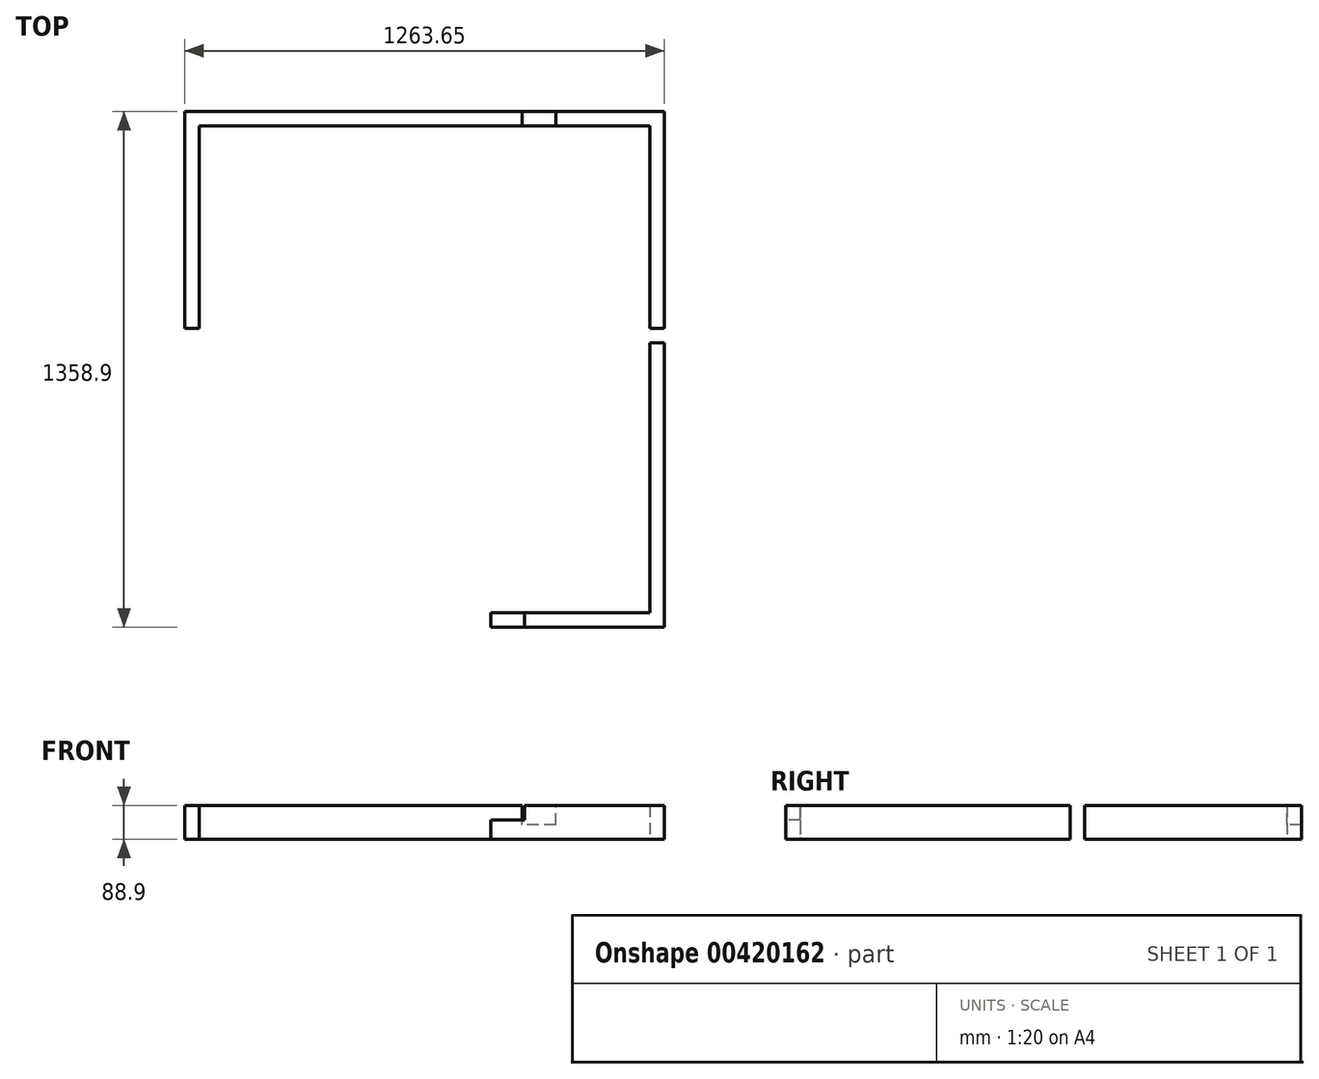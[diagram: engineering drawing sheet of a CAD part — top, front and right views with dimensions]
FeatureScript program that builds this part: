
annotation { "Feature Type Name" : "Feature", "Feature Type Description" : "" }
export const myFeature = defineFeature(function(context is Context, id is Id, definition is map)
    precondition{}
    {
        {
            var Q0;
            Q0=qCreatedBy(makeId("Top.planeOp"),FACE);
            var sketch = newSketch(context, id + "F0", { "sketchPlane" : qUnion([Q0])});
            skLineSegment(sketch, "E0", {"start": v(0, 0) * mm, "end": v(-1263.65, 0) * mm});
            skLineSegment(sketch, "E1", {"start": v(-1263.65, 0) * mm, "end": v(-1263.65, -609.6) * mm});
            skLineSegment(sketch, "E2", {"start": v(-457.2, -1358.9) * mm, "end": v(0, -1358.9) * mm});
            skLineSegment(sketch, "E3", {"start": v(0, -1358.9) * mm, "end": v(0, 0) * mm});
            skLineSegment(sketch, "E4", {"start": v(-1263.65, -609.6) * mm, "end": v(-457.2, -609.6) * mm});
            skLineSegment(sketch, "E5", {"start": v(-457.2, -609.6) * mm, "end": v(-457.2, -1358.9) * mm});
            skLineSegment(sketch, "E6.0", {"start": v(-1225.55, -38.1) * mm, "end": v(-1225.55, -609.6) * mm});
            skLineSegment(sketch, "E6.1", {"start": v(-38.1, -38.1) * mm, "end": v(-1225.55, -38.1) * mm});
            skLineSegment(sketch, "E6.2", {"start": v(-38.1, -1320.8) * mm, "end": v(-38.1, -38.1) * mm});
            skLineSegment(sketch, "E6.3", {"start": v(-457.2, -1320.8) * mm, "end": v(-38.1, -1320.8) * mm});
            skLineSegment(sketch, "E7", {"start": v(-1225.55, -609.6) * mm, "end": v(-1263.65, -609.6) * mm});
            skLineSegment(sketch, "E8", {"start": v(-457.2, -1320.8) * mm, "end": v(-457.2, -1358.9) * mm});
            skSolve(sketch);
        }
        {
            var Q0;
            Q0=makeQuery(id+"F0.imprint","IMPRINT",FACE,{"disambiguationData":[TD([[makeQuery(id+"F0.imprint","IMPRINT",EDGE,{"derivedFrom":sQuery(id+"F0.wireOp",EDGE,"E0")}),1.0]])]});
            extrude(context, id + "F1", {"entities" : qUnion([Q0]), "depth" : 88.9 * mm});
        }
        {
            var Q0;
            Q0=makeQuery(id+"F1.opExtrude","CAP_FACE",FACE,{"disambiguationData":[OSD([sQuery(id+"F0.wireOp",EDGE,"E0"),sQuery(id+"F0.wireOp",EDGE,"E1"),sQuery(id+"F0.wireOp",EDGE,"E2"),sQuery(id+"F0.wireOp",EDGE,"E3"),sQuery(id+"F0.wireOp",EDGE,"E6.0"),sQuery(id+"F0.wireOp",EDGE,"E6.1"),sQuery(id+"F0.wireOp",EDGE,"E6.2"),sQuery(id+"F0.wireOp",EDGE,"E6.3"),sQuery(id+"F0.wireOp",EDGE,"E7"),sQuery(id+"F0.wireOp",EDGE,"E8")])],"isStart":false});
            var sketch = newSketch(context, id + "F2", { "sketchPlane" : qUnion([Q0])});
            skLineSegment(sketch, "E9.bottom", {"start": v(-1263.65, -609.6) * mm, "end": v(0, -609.6) * mm});
            skLineSegment(sketch, "E9.top", {"start": v(-1263.65, -571.5) * mm, "end": v(0, -571.5) * mm});
            skLineSegment(sketch, "E9.left", {"start": v(-1263.65, -609.6) * mm, "end": v(-1263.65, -571.5) * mm});
            skLineSegment(sketch, "E9.right", {"start": v(0, -609.6) * mm, "end": v(0, -571.5) * mm});
            skSolve(sketch);
        }
        {
            var Q0;
            {var subQ0=sQuery(id+"F2.wireOp",EDGE,"E9.bottom");var subQ3=makeQuery(id+"F1.opExtrude","CAP_EDGE",EDGE,{"disambiguationData":[OSD([sQuery(id+"F0.wireOp",EDGE,"E6.2")])],"isStart":false});var subQ4=makeQuery(id+"F2.imprint","INTERSECT",VERTEX,{"derivedFrom":[subQ3,subQ0]});Q0=makeQuery(id+"F2.imprint","IMPRINT",FACE,{"disambiguationData":[TD([[makeQuery(id+"F2.imprint","IMPRINT",EDGE,{"disambiguationData":[TD([[subQ4,1.0]])],"derivedFrom":subQ0}),1.0]])]});}
            var Q1;
            {var subQ0=sQuery(id+"F2.wireOp",EDGE,"E9.left");Q1=makeQuery(id+"F2.imprint","IMPRINT",FACE,{"disambiguationData":[TD([[makeQuery(id+"F2.imprint","IMPRINT",EDGE,{"derivedFrom":subQ0}),1.0]])]});}
            var Q2;
            {var subQ0=sQuery(id+"F2.wireOp",EDGE,"E9.right");Q2=makeQuery(id+"F2.imprint","IMPRINT",FACE,{"disambiguationData":[TD([[makeQuery(id+"F2.imprint","IMPRINT",EDGE,{"derivedFrom":subQ0}),1.0]])]});}
            extrude(context, id + "F3", {"entities" : qUnion([Q0, Q1, Q2]), "operationType" : NewBodyOperationType.REMOVE, "oppositeDirection" : true, "depth" : 88.9 * mm});
        }
        {
            var Q0;
            {var subQ0=sQuery(id+"F0.wireOp",EDGE,"E6.0");var subQ1=sQuery(id+"F0.wireOp",EDGE,"E1");var subQ2=sQuery(id+"F0.wireOp",EDGE,"E3");var subQ3=sQuery(id+"F0.wireOp",EDGE,"E0");var subQ4=sQuery(id+"F0.wireOp",EDGE,"E6.1");var subQ5=sQuery(id+"F0.wireOp",EDGE,"E6.2");Q0=makeQuery(id+"F3.boolean.opBoolean","SPLIT",FACE,{"disambiguationData":[TD([makeQuery(id+"F1.opExtrude","SWEPT_FACE",FACE,{"disambiguationData":[OSD([subQ3])]})])],"derivedFrom":makeQuery(id+"F1.opExtrude","CAP_FACE",FACE,{"disambiguationData":[OSD([subQ3,subQ1,sQuery(id+"F0.wireOp",EDGE,"E2"),subQ2,subQ0,subQ4,subQ5,sQuery(id+"F0.wireOp",EDGE,"E6.3"),sQuery(id+"F0.wireOp",EDGE,"E7"),sQuery(id+"F0.wireOp",EDGE,"E8")])],"isStart":false})});}
            var sketch = newSketch(context, id + "F4", { "sketchPlane" : qUnion([Q0])});
            skLineSegment(sketch, "E10.bottom", {"start": v(-457.2, -1320.8) * mm, "end": v(-368.3, -1320.8) * mm});
            skLineSegment(sketch, "E10.top", {"start": v(-457.2, -1358.9) * mm, "end": v(-368.3, -1358.9) * mm});
            skLineSegment(sketch, "E10.left", {"start": v(-457.2, -1320.8) * mm, "end": v(-457.2, -1358.9) * mm});
            skLineSegment(sketch, "E10.right", {"start": v(-368.3, -1320.8) * mm, "end": v(-368.3, -1358.9) * mm});
            skSolve(sketch);
        }
        {
            var Q0;
            Q0=makeQuery(id+"F4.imprint","IMPRINT",FACE,{"disambiguationData":[TD([[makeQuery(id+"F4.imprint","IMPRINT",EDGE,{"derivedFrom":sQuery(id+"F4.wireOp",EDGE,"E10.bottom")}),-1.0]])]});
            extrude(context, id + "F5", {"entities" : qUnion([Q0]), "operationType" : NewBodyOperationType.REMOVE, "oppositeDirection" : true, "depth" : 38.1 * mm});
        }
        {
            var Q0;
            {var subQ0=sQuery(id+"F0.wireOp",EDGE,"E6.0");var subQ1=sQuery(id+"F0.wireOp",EDGE,"E1");var subQ2=sQuery(id+"F0.wireOp",EDGE,"E3");var subQ3=sQuery(id+"F0.wireOp",EDGE,"E0");var subQ4=sQuery(id+"F0.wireOp",EDGE,"E6.1");var subQ5=sQuery(id+"F0.wireOp",EDGE,"E6.2");Q0=makeQuery(id+"F3.boolean.opBoolean","SPLIT",FACE,{"disambiguationData":[TD([makeQuery(id+"F1.opExtrude","SWEPT_FACE",FACE,{"disambiguationData":[OSD([subQ3])]})])],"derivedFrom":makeQuery(id+"F1.opExtrude","CAP_FACE",FACE,{"disambiguationData":[OSD([subQ3,subQ1,sQuery(id+"F0.wireOp",EDGE,"E2"),subQ2,subQ0,subQ4,subQ5,sQuery(id+"F0.wireOp",EDGE,"E6.3"),sQuery(id+"F0.wireOp",EDGE,"E7"),sQuery(id+"F0.wireOp",EDGE,"E8")])],"isStart":false})});}
            var sketch = newSketch(context, id + "F6", { "sketchPlane" : qUnion([Q0])});
            skLineSegment(sketch, "E11.bottom", {"start": v(-374.65, 0) * mm, "end": v(-285.75, 0) * mm});
            skLineSegment(sketch, "E11.top", {"start": v(-374.65, -38.1) * mm, "end": v(-285.75, -38.1) * mm});
            skLineSegment(sketch, "E11.left", {"start": v(-374.65, 0) * mm, "end": v(-374.65, -38.1) * mm});
            skLineSegment(sketch, "E11.right", {"start": v(-285.75, 0) * mm, "end": v(-285.75, -38.1) * mm});
            skSolve(sketch);
        }
        {
            var Q0;
            Q0 = qSketchRegion(id + "F6", true);
            extrude(context, id + "F7", {"entities" : qUnion([Q0]), "operationType" : NewBodyOperationType.REMOVE, "oppositeDirection" : true, "depth" : 50.8 * mm});
        }
    });
